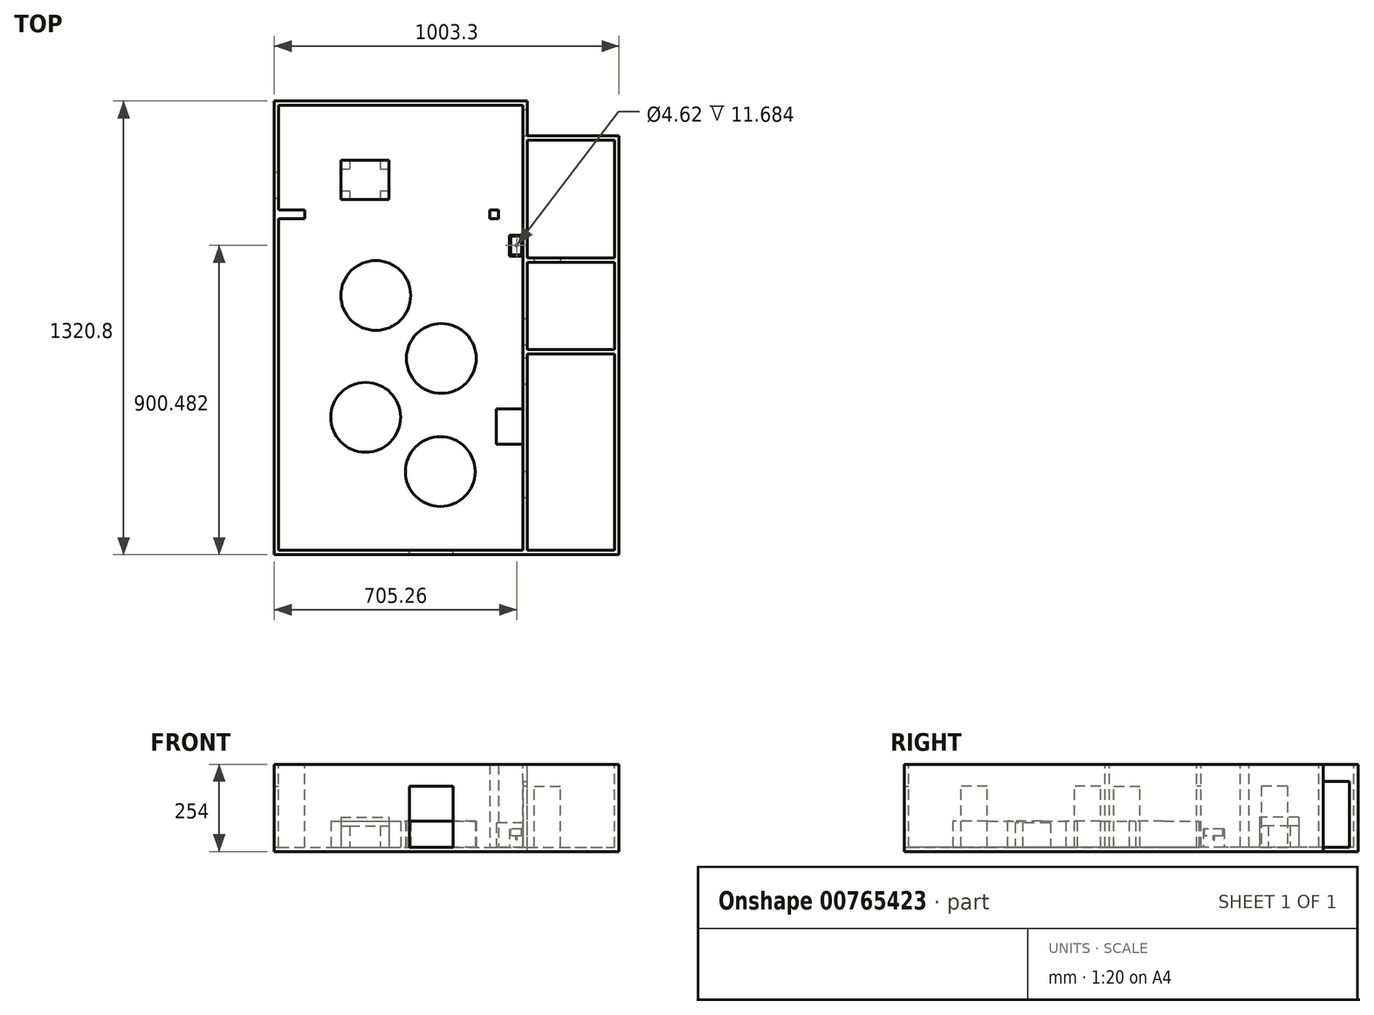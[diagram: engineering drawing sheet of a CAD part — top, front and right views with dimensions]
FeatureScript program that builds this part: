
annotation { "Feature Type Name" : "Feature", "Feature Type Description" : "" }
export const myFeature = defineFeature(function(context is Context, id is Id, definition is map)
    precondition{}
    {
        {
            var Q0;
            Q0=qCreatedBy(makeId("Top.planeOp"),FACE);
            var sketch = newSketch(context, id + "F0", { "sketchPlane" : qUnion([Q0])});
            skLineSegment(sketch, "E0.bottom", {"start": v(-692.56, 541.58) * mm, "end": v(18.64, 541.58) * mm});
            skLineSegment(sketch, "E0.top", {"start": v(-692.56, -753.82) * mm, "end": v(18.64, -753.82) * mm});
            skLineSegment(sketch, "E0.left", {"start": v(-692.56, 541.58) * mm, "end": v(-692.56, -753.82) * mm});
            skLineSegment(sketch, "E0.right", {"start": v(18.64, 541.58) * mm, "end": v(18.64, -753.82) * mm});
            skLineSegment(sketch, "E1.0", {"start": v(-578.26, -766.52) * mm, "end": v(31.34, -766.52) * mm});
            skLineSegment(sketch, "E2.0", {"start": v(31.34, 554.28) * mm, "end": v(31.34, -639.52) * mm});
            skLineSegment(sketch, "E3.0", {"start": v(-578.26, 554.28) * mm, "end": v(31.34, 554.28) * mm});
            skLineSegment(sketch, "E4.0", {"start": v(-705.26, 554.28) * mm, "end": v(-705.26, -639.52) * mm});
            skLineSegment(sketch, "E5", {"start": v(-705.26, -766.52) * mm, "end": v(-578.26, -766.52) * mm});
            skLineSegment(sketch, "E6", {"start": v(-705.26, -766.52) * mm, "end": v(-705.26, -639.52) * mm});
            skLineSegment(sketch, "E7", {"start": v(31.34, -766.52) * mm, "end": v(31.34, -639.52) * mm});
            skLineSegment(sketch, "E8", {"start": v(-705.26, 554.28) * mm, "end": v(-578.26, 554.28) * mm});
            skPoint(sketch, "E9.orphan", {"position": v(386.94, 554.28) * mm});
            skPoint(sketch, "E10.orphan", {"position": v(-705.26, 630.48) * mm});
            skLineSegment(sketch, "E11", {"start": v(-692.56, 211.38) * mm, "end": v(-616.93, 211.38) * mm});
            skLineSegment(sketch, "E12", {"start": v(-616.93, 236.78) * mm, "end": v(-616.93, 211.38) * mm});
            skLineSegment(sketch, "E13", {"start": v(-616.93, 236.78) * mm, "end": v(-692.56, 236.78) * mm});
            skLineSegment(sketch, "E14", {"start": v(31.34, -766.52) * mm, "end": v(298.04, -766.52) * mm});
            skLineSegment(sketch, "E15", {"start": v(298.04, -766.52) * mm, "end": v(298.04, 452.68) * mm});
            skLineSegment(sketch, "E16", {"start": v(298.04, 452.68) * mm, "end": v(31.34, 452.68) * mm});
            skLineSegment(sketch, "E17", {"start": v(31.34, -753.82) * mm, "end": v(285.34, -753.82) * mm});
            skLineSegment(sketch, "E18", {"start": v(285.34, -753.82) * mm, "end": v(285.34, 439.98) * mm});
            skLineSegment(sketch, "E19", {"start": v(285.34, 439.98) * mm, "end": v(31.34, 439.98) * mm});
            skLineSegment(sketch, "E20", {"start": v(31.34, 97.08) * mm, "end": v(285.34, 97.08) * mm});
            skLineSegment(sketch, "E21", {"start": v(31.34, 84.38) * mm, "end": v(285.34, 84.38) * mm});
            skLineSegment(sketch, "E22", {"start": v(31.34, -169.62) * mm, "end": v(285.34, -169.62) * mm});
            skLineSegment(sketch, "E23", {"start": v(31.34, -182.32) * mm, "end": v(285.34, -182.32) * mm});
            skSolve(sketch);
        }
        {
            var Q0;
            Q0 = qSketchRegion(id + "F0", true);
            var Q1;
            {var subQ0=sQuery(id+"F0.wireOp",EDGE,"E11");Q1=makeQuery(id+"F0.imprint","IMPRINT",FACE,{"disambiguationData":[TD([[makeQuery(id+"F0.imprint","IMPRINT",EDGE,{"derivedFrom":subQ0}),1.0]])]});}
            var Q2;
            {var subQ0=sQuery(id+"F0.wireOp",EDGE,"E22");Q2=makeQuery(id+"F0.imprint","IMPRINT",FACE,{"disambiguationData":[TD([[makeQuery(id+"F0.imprint","IMPRINT",EDGE,{"derivedFrom":subQ0}),-1.0]])]});}
            var Q3;
            {var subQ0=sQuery(id+"F0.wireOp",EDGE,"E20");Q3=makeQuery(id+"F0.imprint","IMPRINT",FACE,{"disambiguationData":[TD([[makeQuery(id+"F0.imprint","IMPRINT",EDGE,{"derivedFrom":subQ0}),-1.0]])]});}
            extrude(context, id + "F1", {"entities" : qUnion([Q0, Q1, Q2, Q3]), "oppositeDirection" : true, "depth" : 254 * mm, "offsetDistance" : 25.4 * mm});
        }
        {
            var Q0;
            Q0=makeQuery(id+"F1.opExtrude","CAP_FACE",FACE,{"disambiguationData":[OSD([sQuery(id+"F0.wireOp",EDGE,"E0.bottom"),sQuery(id+"F0.wireOp",EDGE,"E0.top"),sQuery(id+"F0.wireOp",EDGE,"E0.left"),sQuery(id+"F0.wireOp",EDGE,"E0.right"),sQuery(id+"F0.wireOp",EDGE,"E1.0"),sQuery(id+"F0.wireOp",EDGE,"E2.0"),sQuery(id+"F0.wireOp",EDGE,"E3.0"),sQuery(id+"F0.wireOp",EDGE,"E4.0"),sQuery(id+"F0.wireOp",EDGE,"E5"),sQuery(id+"F0.wireOp",EDGE,"E6"),sQuery(id+"F0.wireOp",EDGE,"E7"),sQuery(id+"F0.wireOp",EDGE,"E8"),sQuery(id+"F0.wireOp",EDGE,"E11"),sQuery(id+"F0.wireOp",EDGE,"E12"),sQuery(id+"F0.wireOp",EDGE,"E13"),sQuery(id+"F0.wireOp",EDGE,"E14"),sQuery(id+"F0.wireOp",EDGE,"E15"),sQuery(id+"F0.wireOp",EDGE,"E16"),sQuery(id+"F0.wireOp",EDGE,"E17"),sQuery(id+"F0.wireOp",EDGE,"E18"),sQuery(id+"F0.wireOp",EDGE,"E19"),sQuery(id+"F0.wireOp",EDGE,"E20"),sQuery(id+"F0.wireOp",EDGE,"E21"),sQuery(id+"F0.wireOp",EDGE,"E22"),sQuery(id+"F0.wireOp",EDGE,"E23")])],"isStart":false});
            var sketch = newSketch(context, id + "F2", { "sketchPlane" : qUnion([Q0])});
            skLineSegment(sketch, "E24", {"start": v(-692.56, -554.28) * mm, "end": v(31.34, -554.28) * mm});
            skLineSegment(sketch, "E25", {"start": v(31.34, -452.68) * mm, "end": v(31.34, -554.28) * mm});
            skLineSegment(sketch, "E26", {"start": v(31.34, -452.68) * mm, "end": v(298.04, -452.68) * mm});
            skLineSegment(sketch, "E27", {"start": v(298.04, 766.52) * mm, "end": v(298.04, -452.68) * mm});
            skLineSegment(sketch, "E28", {"start": v(298.04, 766.52) * mm, "end": v(-705.26, 766.52) * mm});
            skLineSegment(sketch, "E29", {"start": v(-705.26, -554.28) * mm, "end": v(-705.26, 766.52) * mm});
            skLineSegment(sketch, "E30", {"start": v(-705.26, -554.28) * mm, "end": v(-692.56, -554.28) * mm});
            skSolve(sketch);
        }
        {
            var Q0;
            Q0 = qSketchRegion(id + "F2", true);
            extrude(context, id + "F3", {"entities" : qUnion([Q0]), "operationType" : NewBodyOperationType.ADD, "oppositeDirection" : true, "depth" : 12.7 * mm, "offsetDistance" : 25.4 * mm});
        }
        {
            var Q0;
            {var subQ1=sQuery(id+"F0.wireOp",EDGE,"E0.bottom");Q0=makeQuery(id+"F3.boolean.opBoolean","SPLIT",FACE,{"disambiguationData":[TD([makeQuery(id+"F1.opExtrude","SWEPT_FACE",FACE,{"disambiguationData":[OSD([subQ1])]})])],"derivedFrom":makeQuery(id+"F3.opExtrude","CAP_FACE",FACE,{"disambiguationData":[OSD([sQuery(id+"F2.wireOp",EDGE,"E24"),sQuery(id+"F2.wireOp",EDGE,"E25"),sQuery(id+"F2.wireOp",EDGE,"E26"),sQuery(id+"F2.wireOp",EDGE,"E27"),sQuery(id+"F2.wireOp",EDGE,"E28"),sQuery(id+"F2.wireOp",EDGE,"E29"),sQuery(id+"F2.wireOp",EDGE,"E30")])],"isStart":false})});}
            var sketch = newSketch(context, id + "F4", { "sketchPlane" : qUnion([Q0])});
            skCircle(sketch, "E31", {"center": v(-409.72, -11.72) * mm, "radius": 101.6 * mm});
            skCircle(sketch, "E32", {"center": v(-219.13, -194.93) * mm, "radius": 101.6 * mm});
            skCircle(sketch, "E33", {"center": v(-439.27, -366.3) * mm, "radius": 101.6 * mm});
            skCircle(sketch, "E34", {"center": v(-222.09, -524.4) * mm, "radius": 101.6 * mm});
            skSolve(sketch);
        }
        {
            var Q0;
            Q0 = qSketchRegion(id + "F4", true);
            extrude(context, id + "F5", {"entities" : qUnion([Q0]), "operationType" : NewBodyOperationType.ADD, "depth" : 76.2 * mm, "offsetDistance" : 25.4 * mm});
        }
        {
            var Q0;
            {var subQ0=sQuery(id+"F0.wireOp",EDGE,"E0.left");Q0=makeQuery(id+"F1.opExtrude","SWEPT_FACE",FACE,{"disambiguationData":[OSD([subQ0]),TDD([makeQuery(id+"F0.imprint","IMPRINT",EDGE,{"disambiguationData":[TD([[makeQuery(id+"F0.imprint","INTERSECT",VERTEX,{"derivedFrom":[sQuery(id+"F0.wireOp",EDGE,"E0.bottom"),subQ0]}),-1.0]])],"derivedFrom":subQ0})])]});}
            var sketch = newSketch(context, id + "F6", { "sketchPlane" : qUnion([Q0])});
            skLineSegment(sketch, "E35.bottom", {"start": v(271.84, -241.3) * mm, "end": v(348.04, -241.3) * mm});
            skLineSegment(sketch, "E35.top", {"start": v(271.84, -63.5) * mm, "end": v(348.04, -63.5) * mm});
            skLineSegment(sketch, "E35.left", {"start": v(271.84, -241.3) * mm, "end": v(271.84, -63.5) * mm});
            skLineSegment(sketch, "E35.right", {"start": v(348.04, -241.3) * mm, "end": v(348.04, -63.5) * mm});
            skSolve(sketch);
        }
        {
            var Q0;
            Q0 = qSketchRegion(id + "F6", true);
            extrude(context, id + "F7", {"entities" : qUnion([Q0]), "operationType" : NewBodyOperationType.REMOVE, "oppositeDirection" : true, "depth" : 25.4 * mm, "offsetDistance" : 25.4 * mm});
        }
        {
            var Q0;
            Q0=makeQuery(id+"F1.opExtrude","SWEPT_FACE",FACE,{"disambiguationData":[OSD([sQuery(id+"F0.wireOp",EDGE,"E0.top")])]});
            var sketch = newSketch(context, id + "F8", { "sketchPlane" : qUnion([Q0])});
            skLineSegment(sketch, "E36.bottom", {"start": v(184.56, -241.3) * mm, "end": v(311.56, -241.3) * mm});
            skLineSegment(sketch, "E36.top", {"start": v(184.56, -63.5) * mm, "end": v(311.56, -63.5) * mm});
            skLineSegment(sketch, "E36.left", {"start": v(184.56, -241.3) * mm, "end": v(184.56, -63.5) * mm});
            skLineSegment(sketch, "E36.right", {"start": v(311.56, -241.3) * mm, "end": v(311.56, -63.5) * mm});
            skSolve(sketch);
        }
        {
            var Q0;
            Q0 = qSketchRegion(id + "F8", true);
            extrude(context, id + "F9", {"entities" : qUnion([Q0]), "operationType" : NewBodyOperationType.REMOVE, "oppositeDirection" : true, "depth" : 25.4 * mm, "offsetDistance" : 25.4 * mm});
        }
        {
            var Q0;
            Q0=makeQuery(id+"F1.opExtrude","SWEPT_FACE",FACE,{"disambiguationData":[OSD([sQuery(id+"F0.wireOp",EDGE,"E0.right")])]});
            var sketch = newSketch(context, id + "F10", { "sketchPlane" : qUnion([Q0])});
            skLineSegment(sketch, "E37.bottom", {"start": v(195.02, -241.3) * mm, "end": v(271.22, -241.3) * mm});
            skLineSegment(sketch, "E37.top", {"start": v(195.02, -63.5) * mm, "end": v(271.22, -63.5) * mm});
            skLineSegment(sketch, "E37.left", {"start": v(195.02, -241.3) * mm, "end": v(195.02, -63.5) * mm});
            skLineSegment(sketch, "E37.right", {"start": v(271.22, -241.3) * mm, "end": v(271.22, -63.5) * mm});
            skLineSegment(sketch, "E38.bottom", {"start": v(525.22, -241.3) * mm, "end": v(601.42, -241.3) * mm});
            skLineSegment(sketch, "E38.top", {"start": v(525.22, -63.5) * mm, "end": v(601.42, -63.5) * mm});
            skLineSegment(sketch, "E38.left", {"start": v(525.22, -241.3) * mm, "end": v(525.22, -63.5) * mm});
            skLineSegment(sketch, "E38.right", {"start": v(601.42, -241.3) * mm, "end": v(601.42, -63.5) * mm});
            skLineSegment(sketch, "E39.bottom", {"start": v(156.92, -241.3) * mm, "end": v(80.72, -241.3) * mm});
            skLineSegment(sketch, "E39.top", {"start": v(156.92, -63.5) * mm, "end": v(80.72, -63.5) * mm});
            skLineSegment(sketch, "E39.left", {"start": v(156.92, -241.3) * mm, "end": v(156.92, -63.5) * mm});
            skLineSegment(sketch, "E39.right", {"start": v(80.72, -241.3) * mm, "end": v(80.72, -63.5) * mm});
            skSolve(sketch);
        }
        {
            var Q0;
            Q0 = qSketchRegion(id + "F10", true);
            extrude(context, id + "F11", {"entities" : qUnion([Q0]), "operationType" : NewBodyOperationType.REMOVE, "oppositeDirection" : true, "depth" : 25.4 * mm, "offsetDistance" : 25.4 * mm});
        }
        {
            var Q0;
            Q0=makeQuery(id+"F1.opExtrude","SWEPT_FACE",FACE,{"disambiguationData":[OSD([sQuery(id+"F0.wireOp",EDGE,"E21")])]});
            var sketch = newSketch(context, id + "F12", { "sketchPlane" : qUnion([Q0])});
            skLineSegment(sketch, "E40.bottom", {"start": v(50.97, -241.3) * mm, "end": v(127.17, -241.3) * mm});
            skLineSegment(sketch, "E40.top", {"start": v(50.97, -63.5) * mm, "end": v(127.17, -63.5) * mm});
            skLineSegment(sketch, "E40.left", {"start": v(50.97, -241.3) * mm, "end": v(50.97, -63.5) * mm});
            skLineSegment(sketch, "E40.right", {"start": v(127.17, -241.3) * mm, "end": v(127.17, -63.5) * mm});
            skSolve(sketch);
        }
        {
            var Q0;
            Q0 = qSketchRegion(id + "F12", true);
            extrude(context, id + "F13", {"entities" : qUnion([Q0]), "operationType" : NewBodyOperationType.REMOVE, "oppositeDirection" : true, "depth" : 25.4 * mm, "offsetDistance" : 25.4 * mm});
        }
        {
            var Q0;
            {var subQ0=sQuery(id+"F0.wireOp",EDGE,"E2.0");Q0=makeQuery(id+"F1.opExtrude","SWEPT_FACE",FACE,{"disambiguationData":[OSD([subQ0]),TDD([makeQuery(id+"F0.imprint","IMPRINT",EDGE,{"disambiguationData":[TD([[makeQuery(id+"F0.imprint","INTERSECT",VERTEX,{"derivedFrom":[subQ0,sQuery(id+"F0.wireOp",EDGE,"E3.0")]}),-1.0]])],"derivedFrom":subQ0})])]});}
            var sketch = newSketch(context, id + "F14", { "sketchPlane" : qUnion([Q0])});
            skLineSegment(sketch, "E41.bottom", {"start": v(528.88, -241.3) * mm, "end": v(452.68, -241.3) * mm});
            skLineSegment(sketch, "E41.top", {"start": v(528.88, -49.94) * mm, "end": v(452.68, -49.94) * mm});
            skLineSegment(sketch, "E41.left", {"start": v(528.88, -241.3) * mm, "end": v(528.88, -49.94) * mm});
            skLineSegment(sketch, "E41.right", {"start": v(452.68, -241.3) * mm, "end": v(452.68, -49.94) * mm});
            skSolve(sketch);
        }
        {
            var Q0;
            Q0 = qSketchRegion(id + "F14", true);
            extrude(context, id + "F15", {"entities" : qUnion([Q0]), "operationType" : NewBodyOperationType.REMOVE, "oppositeDirection" : true, "depth" : 25.4 * mm, "offsetDistance" : 25.4 * mm});
        }
        {
            var Q0;
            {var subQ1=sQuery(id+"F0.wireOp",EDGE,"E0.bottom");var subQ5=makeQuery(id+"F3.opExtrude","CAP_FACE",FACE,{"disambiguationData":[OSD([sQuery(id+"F2.wireOp",EDGE,"E24"),sQuery(id+"F2.wireOp",EDGE,"E25"),sQuery(id+"F2.wireOp",EDGE,"E26"),sQuery(id+"F2.wireOp",EDGE,"E27"),sQuery(id+"F2.wireOp",EDGE,"E28"),sQuery(id+"F2.wireOp",EDGE,"E29"),sQuery(id+"F2.wireOp",EDGE,"E30")])],"isStart":false});var subQ7=sQuery(id+"F0.wireOp",EDGE,"E17");var subQ10=sQuery(id+"F0.wireOp",EDGE,"E21");var subQ12=sQuery(id+"F0.wireOp",EDGE,"E19");Q0=makeQuery(id+"F15.boolean.opBoolean","MERGE",FACE,{"derivedFrom":[makeQuery(id+"F13.boolean.opBoolean","MERGE",FACE,{"derivedFrom":[makeQuery(id+"F3.boolean.opBoolean","SPLIT",FACE,{"disambiguationData":[TD([makeQuery(id+"F1.opExtrude","SWEPT_FACE",FACE,{"disambiguationData":[OSD([subQ12])]})])],"derivedFrom":subQ5}),makeQuery(id+"F11.boolean.opBoolean","MERGE",FACE,{"derivedFrom":[makeQuery(id+"F3.boolean.opBoolean","SPLIT",FACE,{"disambiguationData":[TD([makeQuery(id+"F1.opExtrude","SWEPT_FACE",FACE,{"disambiguationData":[OSD([subQ10])]})])],"derivedFrom":subQ5}),makeQuery(id+"F3.boolean.opBoolean","SPLIT",FACE,{"disambiguationData":[TD([makeQuery(id+"F1.opExtrude","SWEPT_FACE",FACE,{"disambiguationData":[OSD([subQ7])]})])],"derivedFrom":subQ5}),makeQuery(id+"F9.boolean.opBoolean","MERGE",FACE,{"derivedFrom":[makeQuery(id+"F7.boolean.opBoolean","MERGE",FACE,{"derivedFrom":[makeQuery(id+"F3.boolean.opBoolean","SPLIT",FACE,{"disambiguationData":[TD([makeQuery(id+"F1.opExtrude","SWEPT_FACE",FACE,{"disambiguationData":[OSD([subQ1])]})])],"derivedFrom":subQ5}),makeQuery(id+"F7.opExtrude","SWEPT_FACE",FACE,{"disambiguationData":[OSD([sQuery(id+"F6.wireOp",EDGE,"E35.bottom")])]})]}),makeQuery(id+"F9.opExtrude","SWEPT_FACE",FACE,{"disambiguationData":[OSD([sQuery(id+"F8.wireOp",EDGE,"E36.bottom")])]})]}),makeQuery(id+"F11.opExtrude","SWEPT_FACE",FACE,{"disambiguationData":[OSD([sQuery(id+"F10.wireOp",EDGE,"E37.bottom")])]}),makeQuery(id+"F11.opExtrude","SWEPT_FACE",FACE,{"disambiguationData":[OSD([sQuery(id+"F10.wireOp",EDGE,"E38.bottom")])]}),makeQuery(id+"F11.opExtrude","SWEPT_FACE",FACE,{"disambiguationData":[OSD([sQuery(id+"F10.wireOp",EDGE,"E39.bottom")])]})]}),makeQuery(id+"F13.opExtrude","SWEPT_FACE",FACE,{"disambiguationData":[OSD([sQuery(id+"F12.wireOp",EDGE,"E40.bottom")])]})]}),makeQuery(id+"F15.opExtrude","SWEPT_FACE",FACE,{"disambiguationData":[OSD([sQuery(id+"F14.wireOp",EDGE,"E41.bottom")])]})]});}
            var sketch = newSketch(context, id + "F16", { "sketchPlane" : qUnion([Q0])});
            skLineSegment(sketch, "E42", {"start": v(-78.7, 281.55) * mm, "end": v(-78.7, 177.3) * mm});
            skPoint(sketch, "E43.end.orphan", {"position": v(-78.7, 236.78) * mm});
            skLineSegment(sketch, "E44", {"start": v(-616.93, 211.38) * mm, "end": v(-61.15, 211.38) * mm});
            skLineSegment(sketch, "E45.bottom", {"start": v(-78.7, 211.38) * mm, "end": v(-53.3, 211.38) * mm});
            skLineSegment(sketch, "E45.top", {"start": v(-78.7, 236.78) * mm, "end": v(-53.3, 236.78) * mm});
            skLineSegment(sketch, "E45.left", {"start": v(-78.7, 211.38) * mm, "end": v(-78.7, 236.78) * mm});
            skLineSegment(sketch, "E45.right", {"start": v(-53.3, 211.38) * mm, "end": v(-53.3, 236.78) * mm});
            skSolve(sketch);
        }
        {
            var Q0;
            Q0 = qSketchRegion(id + "F16", true);
            extrude(context, id + "F17", {"entities" : qUnion([Q0]), "operationType" : NewBodyOperationType.ADD, "depth" : 241.3 * mm, "offsetDistance" : 25.4 * mm});
        }
        {
            var Q0;
            {var subQ1=sQuery(id+"F0.wireOp",EDGE,"E0.bottom");var subQ5=makeQuery(id+"F3.opExtrude","CAP_FACE",FACE,{"disambiguationData":[OSD([sQuery(id+"F2.wireOp",EDGE,"E24"),sQuery(id+"F2.wireOp",EDGE,"E25"),sQuery(id+"F2.wireOp",EDGE,"E26"),sQuery(id+"F2.wireOp",EDGE,"E27"),sQuery(id+"F2.wireOp",EDGE,"E28"),sQuery(id+"F2.wireOp",EDGE,"E29"),sQuery(id+"F2.wireOp",EDGE,"E30")])],"isStart":false});var subQ7=sQuery(id+"F0.wireOp",EDGE,"E17");var subQ10=sQuery(id+"F0.wireOp",EDGE,"E21");var subQ12=sQuery(id+"F0.wireOp",EDGE,"E19");Q0=makeQuery(id+"F15.boolean.opBoolean","MERGE",FACE,{"derivedFrom":[makeQuery(id+"F13.boolean.opBoolean","MERGE",FACE,{"derivedFrom":[makeQuery(id+"F3.boolean.opBoolean","SPLIT",FACE,{"disambiguationData":[TD([makeQuery(id+"F1.opExtrude","SWEPT_FACE",FACE,{"disambiguationData":[OSD([subQ12])]})])],"derivedFrom":subQ5}),makeQuery(id+"F11.boolean.opBoolean","MERGE",FACE,{"derivedFrom":[makeQuery(id+"F3.boolean.opBoolean","SPLIT",FACE,{"disambiguationData":[TD([makeQuery(id+"F1.opExtrude","SWEPT_FACE",FACE,{"disambiguationData":[OSD([subQ10])]})])],"derivedFrom":subQ5}),makeQuery(id+"F3.boolean.opBoolean","SPLIT",FACE,{"disambiguationData":[TD([makeQuery(id+"F1.opExtrude","SWEPT_FACE",FACE,{"disambiguationData":[OSD([subQ7])]})])],"derivedFrom":subQ5}),makeQuery(id+"F9.boolean.opBoolean","MERGE",FACE,{"derivedFrom":[makeQuery(id+"F7.boolean.opBoolean","MERGE",FACE,{"derivedFrom":[makeQuery(id+"F3.boolean.opBoolean","SPLIT",FACE,{"disambiguationData":[TD([makeQuery(id+"F1.opExtrude","SWEPT_FACE",FACE,{"disambiguationData":[OSD([subQ1])]})])],"derivedFrom":subQ5}),makeQuery(id+"F7.opExtrude","SWEPT_FACE",FACE,{"disambiguationData":[OSD([sQuery(id+"F6.wireOp",EDGE,"E35.bottom")])]})]}),makeQuery(id+"F9.opExtrude","SWEPT_FACE",FACE,{"disambiguationData":[OSD([sQuery(id+"F8.wireOp",EDGE,"E36.bottom")])]})]}),makeQuery(id+"F11.opExtrude","SWEPT_FACE",FACE,{"disambiguationData":[OSD([sQuery(id+"F10.wireOp",EDGE,"E37.bottom")])]}),makeQuery(id+"F11.opExtrude","SWEPT_FACE",FACE,{"disambiguationData":[OSD([sQuery(id+"F10.wireOp",EDGE,"E38.bottom")])]}),makeQuery(id+"F11.opExtrude","SWEPT_FACE",FACE,{"disambiguationData":[OSD([sQuery(id+"F10.wireOp",EDGE,"E39.bottom")])]})]}),makeQuery(id+"F13.opExtrude","SWEPT_FACE",FACE,{"disambiguationData":[OSD([sQuery(id+"F12.wireOp",EDGE,"E40.bottom")])]})]}),makeQuery(id+"F15.opExtrude","SWEPT_FACE",FACE,{"disambiguationData":[OSD([sQuery(id+"F14.wireOp",EDGE,"E41.bottom")])]})]});}
            var sketch = newSketch(context, id + "F18", { "sketchPlane" : qUnion([Q0])});
            skLineSegment(sketch, "E46.bottom", {"start": v(-511.67, 381.63) * mm, "end": v(-486.27, 381.63) * mm});
            skLineSegment(sketch, "E46.top", {"start": v(-511.67, 356.23) * mm, "end": v(-486.27, 356.23) * mm});
            skLineSegment(sketch, "E46.left", {"start": v(-511.67, 381.63) * mm, "end": v(-511.67, 356.23) * mm});
            skLineSegment(sketch, "E46.right", {"start": v(-486.27, 381.63) * mm, "end": v(-486.27, 356.23) * mm});
            skLineSegment(sketch, "E47.bottom", {"start": v(-511.67, 292.7) * mm, "end": v(-486.27, 292.7) * mm});
            skLineSegment(sketch, "E47.top", {"start": v(-511.67, 267.3) * mm, "end": v(-486.27, 267.3) * mm});
            skLineSegment(sketch, "E47.left", {"start": v(-511.67, 292.7) * mm, "end": v(-511.67, 267.3) * mm});
            skLineSegment(sketch, "E47.right", {"start": v(-486.27, 292.7) * mm, "end": v(-486.27, 267.3) * mm});
            skLineSegment(sketch, "E48.bottom", {"start": v(-396.4, 292.7) * mm, "end": v(-371, 292.7) * mm});
            skLineSegment(sketch, "E48.top", {"start": v(-396.4, 267.3) * mm, "end": v(-371, 267.3) * mm});
            skLineSegment(sketch, "E48.left", {"start": v(-396.4, 292.7) * mm, "end": v(-396.4, 267.3) * mm});
            skLineSegment(sketch, "E48.right", {"start": v(-371, 292.7) * mm, "end": v(-371, 267.3) * mm});
            skLineSegment(sketch, "E49.bottom", {"start": v(-396.4, 381.63) * mm, "end": v(-371, 381.63) * mm});
            skLineSegment(sketch, "E49.top", {"start": v(-396.4, 356.23) * mm, "end": v(-371, 356.23) * mm});
            skLineSegment(sketch, "E49.left", {"start": v(-396.4, 381.63) * mm, "end": v(-396.4, 356.23) * mm});
            skLineSegment(sketch, "E49.right", {"start": v(-371, 381.63) * mm, "end": v(-371, 356.23) * mm});
            skSolve(sketch);
        }
        {
            var Q0;
            Q0 = qSketchRegion(id + "F18", true);
            extrude(context, id + "F19", {"entities" : qUnion([Q0]), "operationType" : NewBodyOperationType.ADD, "depth" : 62.23 * mm, "offsetDistance" : 25.4 * mm});
        }
        {
            var Q0;
            Q0 = qSketchRegion(id + "F18", true);
            extrude(context, id + "F20", {"entities" : qUnion([Q0]), "operationType" : NewBodyOperationType.ADD, "depth" : 25.4 * mm, "offsetDistance" : 25.4 * mm});
        }
        {
            var Q0;
            Q0=makeQuery(id+"F19.opExtrude","CAP_FACE",FACE,{"disambiguationData":[OSD([sQuery(id+"F18.wireOp",EDGE,"E46.bottom"),sQuery(id+"F18.wireOp",EDGE,"E46.top"),sQuery(id+"F18.wireOp",EDGE,"E46.left"),sQuery(id+"F18.wireOp",EDGE,"E46.right")])],"isStart":false});
            var sketch = newSketch(context, id + "F21", { "sketchPlane" : qUnion([Q0])});
            skLineSegment(sketch, "E50.0.0", {"start": v(-511.67, 381.63) * mm, "end": v(-511.67, 356.23) * mm});
            skLineSegment(sketch, "E50.0.1", {"start": v(-511.67, 356.23) * mm, "end": v(-486.27, 356.23) * mm});
            skLineSegment(sketch, "E50.0.2", {"start": v(-486.27, 356.23) * mm, "end": v(-486.27, 381.63) * mm});
            skLineSegment(sketch, "E50.0.3", {"start": v(-486.27, 381.63) * mm, "end": v(-511.67, 381.63) * mm});
            skLineSegment(sketch, "E51.0.0", {"start": v(-396.4, 292.7) * mm, "end": v(-396.4, 267.3) * mm});
            skLineSegment(sketch, "E51.0.1", {"start": v(-396.4, 267.3) * mm, "end": v(-371, 267.3) * mm});
            skLineSegment(sketch, "E51.0.2", {"start": v(-371, 267.3) * mm, "end": v(-371, 292.7) * mm});
            skLineSegment(sketch, "E51.0.3", {"start": v(-371, 292.7) * mm, "end": v(-396.4, 292.7) * mm});
            skLineSegment(sketch, "E52.bottom", {"start": v(-511.67, 381.63) * mm, "end": v(-371, 381.63) * mm});
            skLineSegment(sketch, "E52.top", {"start": v(-511.67, 267.3) * mm, "end": v(-371, 267.3) * mm});
            skLineSegment(sketch, "E52.left", {"start": v(-511.67, 381.63) * mm, "end": v(-511.67, 267.3) * mm});
            skLineSegment(sketch, "E52.right", {"start": v(-371, 381.63) * mm, "end": v(-371, 267.3) * mm});
            skSolve(sketch);
        }
        {
            var Q0;
            Q0 = qSketchRegion(id + "F21", true);
            extrude(context, id + "F22", {"entities" : qUnion([Q0]), "operationType" : NewBodyOperationType.ADD, "depth" : 25.4 * mm, "offsetDistance" : 25.4 * mm});
        }
        {
            var Q0;
            {var subQ1=sQuery(id+"F0.wireOp",EDGE,"E0.bottom");var subQ5=makeQuery(id+"F3.opExtrude","CAP_FACE",FACE,{"disambiguationData":[OSD([sQuery(id+"F2.wireOp",EDGE,"E24"),sQuery(id+"F2.wireOp",EDGE,"E25"),sQuery(id+"F2.wireOp",EDGE,"E26"),sQuery(id+"F2.wireOp",EDGE,"E27"),sQuery(id+"F2.wireOp",EDGE,"E28"),sQuery(id+"F2.wireOp",EDGE,"E29"),sQuery(id+"F2.wireOp",EDGE,"E30")])],"isStart":false});var subQ7=sQuery(id+"F0.wireOp",EDGE,"E17");var subQ10=sQuery(id+"F0.wireOp",EDGE,"E21");var subQ12=sQuery(id+"F0.wireOp",EDGE,"E19");Q0=makeQuery(id+"F15.boolean.opBoolean","MERGE",FACE,{"derivedFrom":[makeQuery(id+"F13.boolean.opBoolean","MERGE",FACE,{"derivedFrom":[makeQuery(id+"F3.boolean.opBoolean","SPLIT",FACE,{"disambiguationData":[TD([makeQuery(id+"F1.opExtrude","SWEPT_FACE",FACE,{"disambiguationData":[OSD([subQ12])]})])],"derivedFrom":subQ5}),makeQuery(id+"F11.boolean.opBoolean","MERGE",FACE,{"derivedFrom":[makeQuery(id+"F3.boolean.opBoolean","SPLIT",FACE,{"disambiguationData":[TD([makeQuery(id+"F1.opExtrude","SWEPT_FACE",FACE,{"disambiguationData":[OSD([subQ10])]})])],"derivedFrom":subQ5}),makeQuery(id+"F3.boolean.opBoolean","SPLIT",FACE,{"disambiguationData":[TD([makeQuery(id+"F1.opExtrude","SWEPT_FACE",FACE,{"disambiguationData":[OSD([subQ7])]})])],"derivedFrom":subQ5}),makeQuery(id+"F9.boolean.opBoolean","MERGE",FACE,{"derivedFrom":[makeQuery(id+"F7.boolean.opBoolean","MERGE",FACE,{"derivedFrom":[makeQuery(id+"F3.boolean.opBoolean","SPLIT",FACE,{"disambiguationData":[TD([makeQuery(id+"F1.opExtrude","SWEPT_FACE",FACE,{"disambiguationData":[OSD([subQ1])]})])],"derivedFrom":subQ5}),makeQuery(id+"F7.opExtrude","SWEPT_FACE",FACE,{"disambiguationData":[OSD([sQuery(id+"F6.wireOp",EDGE,"E35.bottom")])]})]}),makeQuery(id+"F9.opExtrude","SWEPT_FACE",FACE,{"disambiguationData":[OSD([sQuery(id+"F8.wireOp",EDGE,"E36.bottom")])]})]}),makeQuery(id+"F11.opExtrude","SWEPT_FACE",FACE,{"disambiguationData":[OSD([sQuery(id+"F10.wireOp",EDGE,"E37.bottom")])]}),makeQuery(id+"F11.opExtrude","SWEPT_FACE",FACE,{"disambiguationData":[OSD([sQuery(id+"F10.wireOp",EDGE,"E38.bottom")])]}),makeQuery(id+"F11.opExtrude","SWEPT_FACE",FACE,{"disambiguationData":[OSD([sQuery(id+"F10.wireOp",EDGE,"E39.bottom")])]})]}),makeQuery(id+"F13.opExtrude","SWEPT_FACE",FACE,{"disambiguationData":[OSD([sQuery(id+"F12.wireOp",EDGE,"E40.bottom")])]})]}),makeQuery(id+"F15.opExtrude","SWEPT_FACE",FACE,{"disambiguationData":[OSD([sQuery(id+"F14.wireOp",EDGE,"E41.bottom")])]})]});}
            var sketch = newSketch(context, id + "F23", { "sketchPlane" : qUnion([Q0])});
            skLineSegment(sketch, "E53.bottom", {"start": v(18.64, -444.56) * mm, "end": v(-58.8, -444.56) * mm});
            skLineSegment(sketch, "E53.top", {"start": v(18.64, -341.95) * mm, "end": v(-58.8, -341.95) * mm});
            skLineSegment(sketch, "E53.left", {"start": v(18.64, -444.56) * mm, "end": v(18.64, -341.95) * mm});
            skLineSegment(sketch, "E53.right", {"start": v(-58.8, -444.56) * mm, "end": v(-58.8, -341.95) * mm});
            skSolve(sketch);
        }
        {
            var Q0;
            Q0 = qSketchRegion(id + "F23", true);
            extrude(context, id + "F24", {"entities" : qUnion([Q0]), "operationType" : NewBodyOperationType.ADD, "depth" : 71.12 * mm, "offsetDistance" : 25.4 * mm});
        }
        {
            var Q0;
            {var subQ1=sQuery(id+"F0.wireOp",EDGE,"E0.bottom");var subQ5=makeQuery(id+"F3.opExtrude","CAP_FACE",FACE,{"disambiguationData":[OSD([sQuery(id+"F2.wireOp",EDGE,"E24"),sQuery(id+"F2.wireOp",EDGE,"E25"),sQuery(id+"F2.wireOp",EDGE,"E26"),sQuery(id+"F2.wireOp",EDGE,"E27"),sQuery(id+"F2.wireOp",EDGE,"E28"),sQuery(id+"F2.wireOp",EDGE,"E29"),sQuery(id+"F2.wireOp",EDGE,"E30")])],"isStart":false});var subQ7=sQuery(id+"F0.wireOp",EDGE,"E17");var subQ10=sQuery(id+"F0.wireOp",EDGE,"E21");var subQ12=sQuery(id+"F0.wireOp",EDGE,"E19");Q0=makeQuery(id+"F15.boolean.opBoolean","MERGE",FACE,{"derivedFrom":[makeQuery(id+"F13.boolean.opBoolean","MERGE",FACE,{"derivedFrom":[makeQuery(id+"F3.boolean.opBoolean","SPLIT",FACE,{"disambiguationData":[TD([makeQuery(id+"F1.opExtrude","SWEPT_FACE",FACE,{"disambiguationData":[OSD([subQ12])]})])],"derivedFrom":subQ5}),makeQuery(id+"F11.boolean.opBoolean","MERGE",FACE,{"derivedFrom":[makeQuery(id+"F3.boolean.opBoolean","SPLIT",FACE,{"disambiguationData":[TD([makeQuery(id+"F1.opExtrude","SWEPT_FACE",FACE,{"disambiguationData":[OSD([subQ10])]})])],"derivedFrom":subQ5}),makeQuery(id+"F3.boolean.opBoolean","SPLIT",FACE,{"disambiguationData":[TD([makeQuery(id+"F1.opExtrude","SWEPT_FACE",FACE,{"disambiguationData":[OSD([subQ7])]})])],"derivedFrom":subQ5}),makeQuery(id+"F9.boolean.opBoolean","MERGE",FACE,{"derivedFrom":[makeQuery(id+"F7.boolean.opBoolean","MERGE",FACE,{"derivedFrom":[makeQuery(id+"F3.boolean.opBoolean","SPLIT",FACE,{"disambiguationData":[TD([makeQuery(id+"F1.opExtrude","SWEPT_FACE",FACE,{"disambiguationData":[OSD([subQ1])]})])],"derivedFrom":subQ5}),makeQuery(id+"F7.opExtrude","SWEPT_FACE",FACE,{"disambiguationData":[OSD([sQuery(id+"F6.wireOp",EDGE,"E35.bottom")])]})]}),makeQuery(id+"F9.opExtrude","SWEPT_FACE",FACE,{"disambiguationData":[OSD([sQuery(id+"F8.wireOp",EDGE,"E36.bottom")])]})]}),makeQuery(id+"F11.opExtrude","SWEPT_FACE",FACE,{"disambiguationData":[OSD([sQuery(id+"F10.wireOp",EDGE,"E37.bottom")])]}),makeQuery(id+"F11.opExtrude","SWEPT_FACE",FACE,{"disambiguationData":[OSD([sQuery(id+"F10.wireOp",EDGE,"E38.bottom")])]}),makeQuery(id+"F11.opExtrude","SWEPT_FACE",FACE,{"disambiguationData":[OSD([sQuery(id+"F10.wireOp",EDGE,"E39.bottom")])]})]}),makeQuery(id+"F13.opExtrude","SWEPT_FACE",FACE,{"disambiguationData":[OSD([sQuery(id+"F12.wireOp",EDGE,"E40.bottom")])]})]}),makeQuery(id+"F15.opExtrude","SWEPT_FACE",FACE,{"disambiguationData":[OSD([sQuery(id+"F14.wireOp",EDGE,"E41.bottom")])]})]});}
            var sketch = newSketch(context, id + "F25", { "sketchPlane" : qUnion([Q0])});
            skLineSegment(sketch, "E54.bottom", {"start": v(18.64, 163.9) * mm, "end": v(-20.73, 163.9) * mm});
            skLineSegment(sketch, "E54.top", {"start": v(18.64, 103.23) * mm, "end": v(-20.73, 103.23) * mm});
            skLineSegment(sketch, "E54.left", {"start": v(18.64, 163.9) * mm, "end": v(18.64, 103.23) * mm});
            skLineSegment(sketch, "E54.right", {"start": v(-20.73, 163.9) * mm, "end": v(-20.73, 103.23) * mm});
            skSolve(sketch);
        }
        {
            var Q0;
            Q0 = qSketchRegion(id + "F25", true);
            extrude(context, id + "F26", {"entities" : qUnion([Q0]), "operationType" : NewBodyOperationType.ADD, "depth" : 53.34 * mm, "offsetDistance" : 25.4 * mm});
        }
        {
            var Q0;
            Q0=makeQuery(id+"F26.opExtrude","CAP_FACE",FACE,{"disambiguationData":[OSD([sQuery(id+"F25.wireOp",EDGE,"E54.bottom"),sQuery(id+"F25.wireOp",EDGE,"E54.top"),sQuery(id+"F25.wireOp",EDGE,"E54.left"),sQuery(id+"F25.wireOp",EDGE,"E54.right")])],"isStart":false});
            var sketch = newSketch(context, id + "F27", { "sketchPlane" : qUnion([Q0])});
            skLineSegment(sketch, "E55.bottom", {"start": v(15.18, 160.66) * mm, "end": v(-17.4, 160.66) * mm});
            skLineSegment(sketch, "E55.top", {"start": v(15.18, 106.46) * mm, "end": v(-17.4, 106.46) * mm});
            skLineSegment(sketch, "E55.left", {"start": v(15.18, 160.66) * mm, "end": v(15.18, 106.46) * mm});
            skLineSegment(sketch, "E55.right", {"start": v(-17.4, 160.66) * mm, "end": v(-17.4, 106.46) * mm});
            skSolve(sketch);
        }
        {
            var Q0;
            Q0 = qSketchRegion(id + "F27", true);
            extrude(context, id + "F28", {"entities" : qUnion([Q0]), "operationType" : NewBodyOperationType.REMOVE, "oppositeDirection" : true, "depth" : 20.32 * mm, "offsetDistance" : 25.4 * mm});
        }
        {
            var Q0;
            Q0=makeQuery(id+"F28.boolean.opBoolean","COPY",FACE,{"derivedFrom":makeQuery(id+"F28.opExtrude","CAP_FACE",FACE,{"disambiguationData":[OSD([sQuery(id+"F27.wireOp",EDGE,"E55.bottom"),sQuery(id+"F27.wireOp",EDGE,"E55.top"),sQuery(id+"F27.wireOp",EDGE,"E55.left"),sQuery(id+"F27.wireOp",EDGE,"E55.right")])],"isStart":false})});
            var sketch = newSketch(context, id + "F29", { "sketchPlane" : qUnion([Q0])});
            skCircle(sketch, "E56", {"center": v(0, 133.96) * mm, "radius": 2.3 * mm});
            skSolve(sketch);
        }
        {
            var Q0;
            Q0 = qSketchRegion(id + "F29", true);
            extrude(context, id + "F30", {"entities" : qUnion([Q0]), "operationType" : NewBodyOperationType.REMOVE, "oppositeDirection" : true, "depth" : 11.68 * mm, "offsetDistance" : 25.4 * mm});
        }
    });
